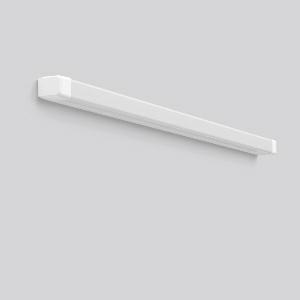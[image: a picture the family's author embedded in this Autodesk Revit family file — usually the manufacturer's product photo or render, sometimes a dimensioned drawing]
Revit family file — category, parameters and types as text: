
# Revit family: baleva_451203_002_2_592f
name_source: partatom
category: Lighting Fixtures
units: mm (PartAtom-declared; Revit-internal decimal feet)

## family parameters
Cut with Voids When Loaded = No
Host = Face
Light Source = No
Part Type = Normal
Room Calculation Point = No
Round Connector Dimension = Use Diameter
Shared = No

## types (1)
- MultiColor 830 (1 x LED Modul 830, 2100 lm, 3000)
    Apparent Load = 19 VA
    CIE Flux Codes = 40 69 88 82 100
    Color Rendering = 80
    Color Temperature = 3000
    Default Elevation = 1800 mm
    Description = Series: BALEVA
Linear luminaire with timeless functional design. Ideal for sanitary areas, corridors, waiting areas, nursing homes, patient rooms. Body and end caps made of white plastic. Diffuser made of plastic (polycarbonate), opal, shockproof. Homogeneous and smooth light distribution. MultiColour: With rear switching element, variable colour temperature 3000  K or 4000  K. Factory setting is 4000 K. Diffuser can be assembled without the use of tools. Quick and easy to install. Can be installed horizontally and vertically. 2 central cable inlets for looping the cable. Converter integrated and encapsulated. 
Colour: white
Length: 1200 mm
Width: 46 mm
Height: 60 mm
Lamp: LED
Socket: without socket
Colour temperature: 3000K, 4000K
Colour rendering index (CRI): 80
System power: 19 W
Rated luminous flux: 2100 lm
Luminous efficiency: 111 lm/W
System power 2: 19 W
Rated luminous flux 2: 2200 lm
Luminous efficiency 2: 116 lm/W
Control gear: Regulated power supply
Protection class: II
Type of protection: IP 40
    Height = 60 mm  [stored 0.19685 ft]
    Lamp = 1 x LED Modul 830
    Lamp Light Flux = 2100 lm
    Lamp count = 1
    Length = 1200 mm
    Lifetime = 50000 h
    Luminous efficacy = 111 lm/W
    Manufacturer = RZB
    ModVariant = No
    Model = 451203.002.2
    Mounting Place = Ceiling, Wall
    Mounting Type = Surface mounted
    Number of Poles = 1
    OnlyDefault = Yes
    Power Factor = 1
    Product Name = BALEVA
    Product group = Surface mounted ceiling and wall luminaires
    ProductGroupID = 305
    Protection Class = Protection class II
    Protection Degree = IP 40
    RLX_Detail_Level = 1
    RLX_Emergency_Light_Flux = 0 lm
    RLX_Emergency_Type = 0
    RLX_Emergency_Type_DB = No
    RlxData = <blob elided: 42641 chars, md5=22739a3c>
    Socket = socket
    Standby Power = 0 W
    System Light Flux = 2100 lm
    System Power = 19 W
    Type Comments = MultiColor 830
    Type Image = 451203.002.jpg
    URL = http://relux.com
    VarID = multicolor_830
    Voltage = 230 V
    Voltage Range = 220-240 V
    Weight = 0.00 kg
    Width = 46 mm

note: [stored X ft] marks values corroborated as IEEE doubles in the binary element streams (Revit-internal decimal feet)

## geometry (parser evidence)
native form markers: Blend x4, Sweep x16
no freeform markers — native parametric forms only
